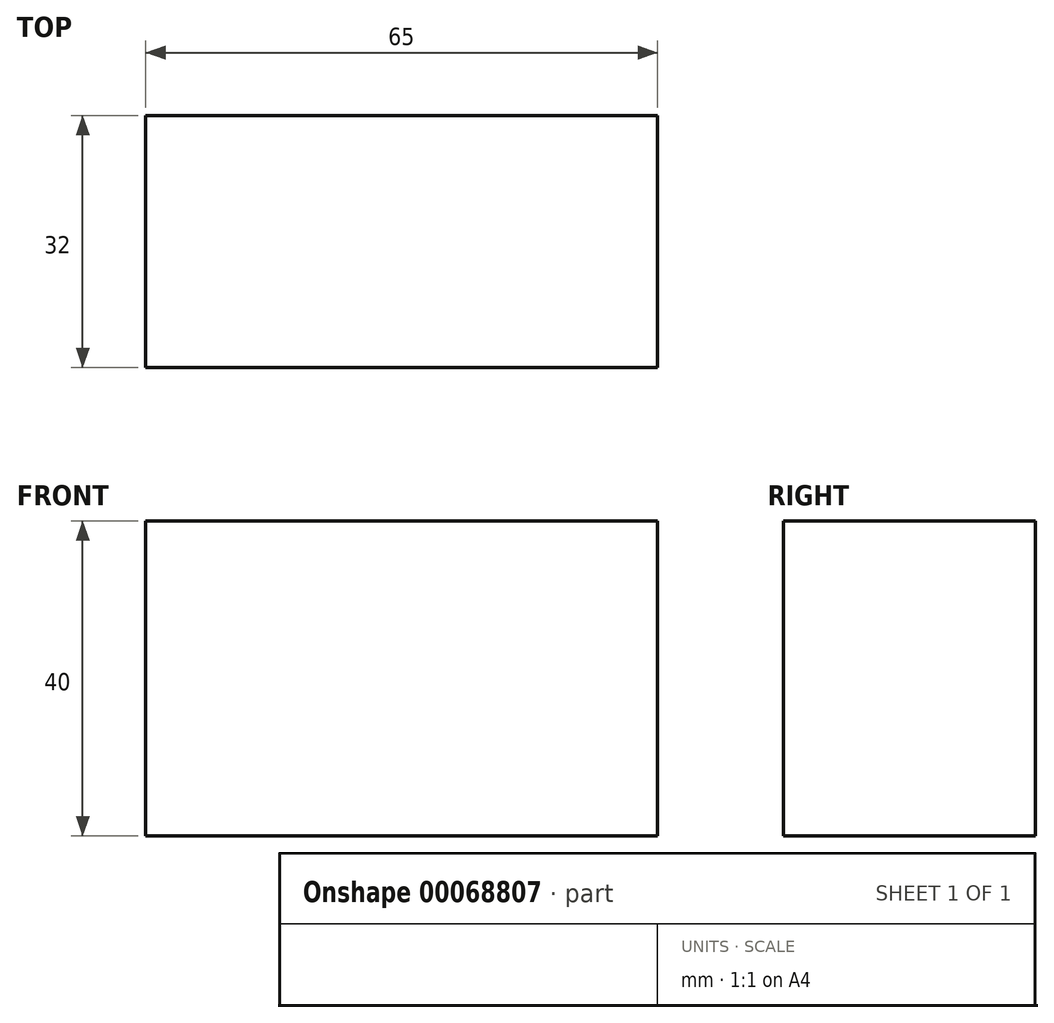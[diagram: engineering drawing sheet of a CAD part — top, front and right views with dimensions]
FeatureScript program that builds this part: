
annotation { "Feature Type Name" : "Feature", "Feature Type Description" : "" }
export const myFeature = defineFeature(function(context is Context, id is Id, definition is map)
    precondition{}
    {
        {
            var Q0;
            Q0=qCreatedBy(makeId("Top.planeOp"),FACE);
            var sketch = newSketch(context, id + "F0", { "sketchPlane" : qUnion([Q0])});
            skLineSegment(sketch, "E0.bottom", {"start": v(0, 0) * mm, "end": v(65, 0) * mm});
            skLineSegment(sketch, "E0.top", {"start": v(0, -32) * mm, "end": v(65, -32) * mm});
            skLineSegment(sketch, "E0.left", {"start": v(0, 0) * mm, "end": v(0, -32) * mm});
            skLineSegment(sketch, "E0.right", {"start": v(65, 0) * mm, "end": v(65, -32) * mm});
            skSolve(sketch);
        }
        {
            var Q0;
            Q0 = qSketchRegion(id + "F0", true);
            extrude(context, id + "F1", {"entities" : qUnion([Q0]), "depth" : 40 * mm});
        }
    });
